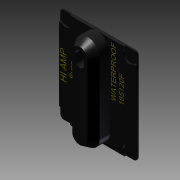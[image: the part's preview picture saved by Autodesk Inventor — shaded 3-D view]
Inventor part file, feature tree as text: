
AUTODESK INVENTOR PART (.ipt)
format: ipt  version: 2013 (Build 170138000, 138)  size: 647,168 bytes
history: native  units: mm (DEFAULTED — no unit token found)
features: sketch x6, extrude x4, plane x2, mirror x2, emboss x2, chamfer x1, reference x1
ambient origin geometry x8: Origin, YZ Plane, XZ Plane, XY Plane, X Axis, Y Axis, Z Axis, Center Point
bodies: Solid1 (feature_tree)
feature tree (18):
  extrude  "Extrusion1"  Depth=6.35mm
  extrude  "Extrusion2"  Depth=3.81mm
  chamfer  "Chamfer2"  Distance=8.89mm
  extrude  "Extrusion3"  Depth=0.762mm
  plane  "Work Plane1"
  plane  "Work Plane2"
  extrude  "Extrusion5"  Depth=0.762mm TaperAngle=0.0deg
  mirror  "Mirror3"
  mirror  "Mirror4"
  emboss  "Emboss1"
  emboss  "Emboss2"
  sketch  "Sketch1"  dims[d0=1.524mm d1=0.0mm d2=6.35mm]
  reference  "Reference1"
  sketch  "Sketch2"  dims[d3=8.89mm d4=0.0mm d7=3.81mm d8=2.54mm]
  sketch  "Sketch3"  dims[d10=2.159mm]
  sketch  "Sketch5"  dims[d11=7.62mm d12=8.89mm d13=0.0mm]
  sketch  "Sketch6"  dims[d17=6.35mm d18=0.762mm]
  sketch  "Sketch7"  dims[d19=0.762mm d20=0.762mm d21=0.0mm d22=0.0508mm d23=0.0mm d24=0.0508mm d25=0.0mm d26=45.0deg]
